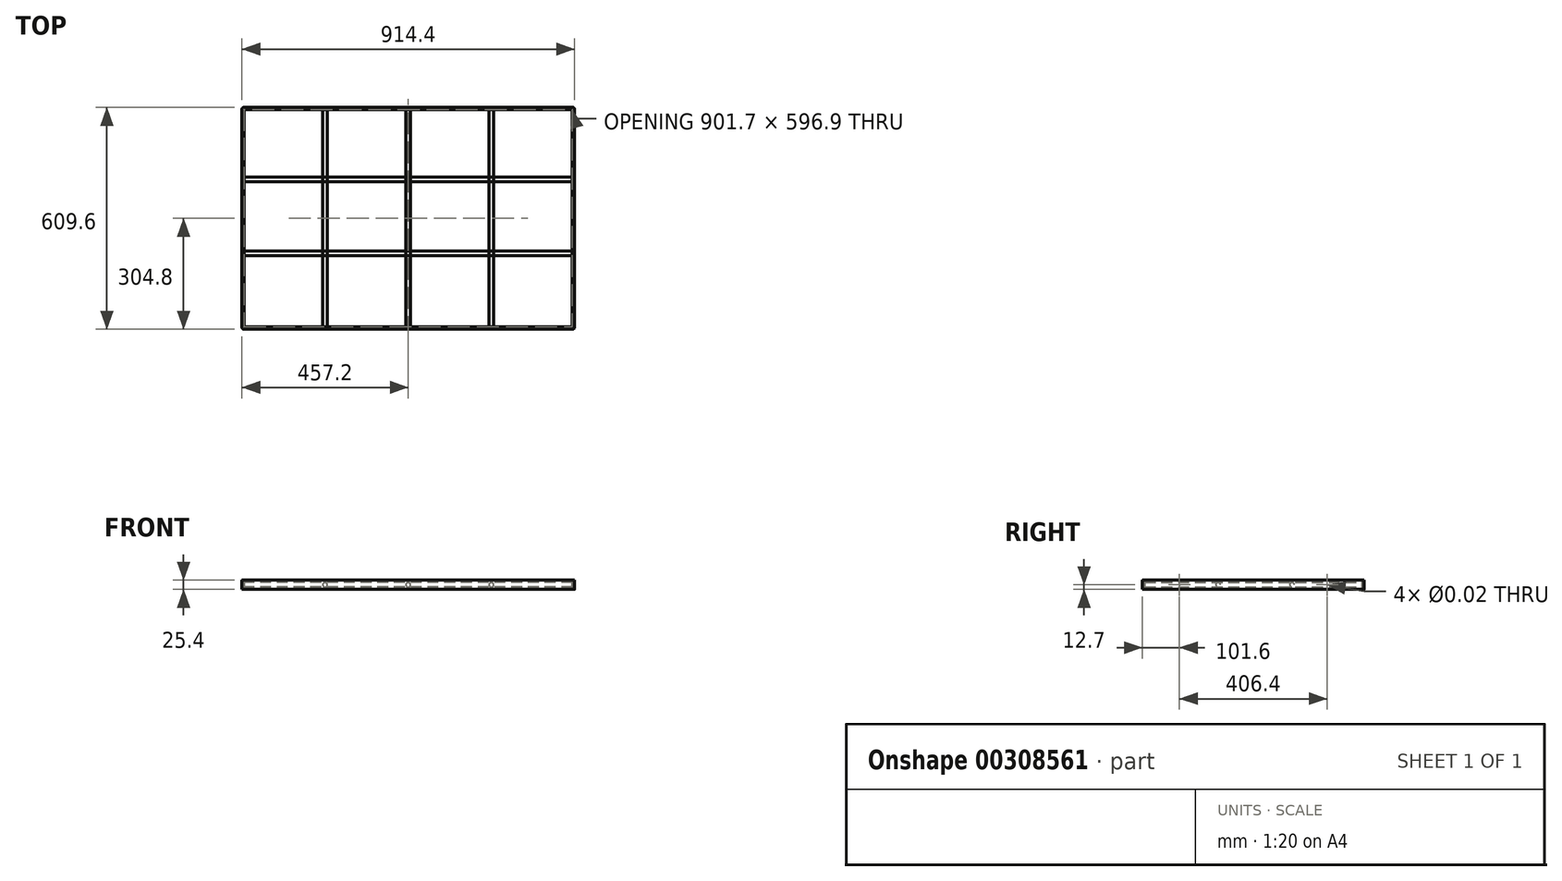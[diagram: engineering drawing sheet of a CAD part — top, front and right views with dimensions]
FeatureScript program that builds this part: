
annotation { "Feature Type Name" : "Feature", "Feature Type Description" : "" }
export const myFeature = defineFeature(function(context is Context, id is Id, definition is map)
    precondition{}
    {
        {
            var Q0;
            Q0=qCreatedBy(makeId("Top.planeOp"),FACE);
            var sketch = newSketch(context, id + "F0", { "sketchPlane" : qUnion([Q0])});
            skLineSegment(sketch, "E0.bottom", {"start": v(0, 0) * mm, "end": v(914.4, 0) * mm});
            skLineSegment(sketch, "E0.top", {"start": v(0, -609.6) * mm, "end": v(914.4, -609.6) * mm});
            skLineSegment(sketch, "E0.left", {"start": v(0, 0) * mm, "end": v(0, -609.6) * mm});
            skLineSegment(sketch, "E0.right", {"start": v(914.4, 0) * mm, "end": v(914.4, -609.6) * mm});
            skLineSegment(sketch, "E1.0", {"start": v(6.35, -6.35) * mm, "end": v(908.05, -6.35) * mm});
            skLineSegment(sketch, "E1.1", {"start": v(6.35, -6.35) * mm, "end": v(6.35, -603.25) * mm});
            skLineSegment(sketch, "E1.2", {"start": v(6.35, -603.25) * mm, "end": v(908.05, -603.25) * mm});
            skLineSegment(sketch, "E1.3", {"start": v(908.05, -6.35) * mm, "end": v(908.05, -603.25) * mm});
            skSolve(sketch);
        }
        {
            var Q0;
            Q0=makeQuery(id+"F0.imprint","IMPRINT",FACE,{"disambiguationData":[TD([[makeQuery(id+"F0.imprint","IMPRINT",EDGE,{"derivedFrom":sQuery(id+"F0.wireOp",EDGE,"E0.bottom")}),-1.0]])]});
            extrude(context, id + "F1", {"entities" : qUnion([Q0]), "depth" : 25.4 * mm});
        }
        {
            var Q0;
            Q0=makeQuery(id+"F1.opExtrude","SWEPT_EDGE",EDGE,{"disambiguationData":[OSD([sQuery(id+"F0.wireOp",EDGE,"E0.bottom"),sQuery(id+"F0.wireOp",EDGE,"E0.right")])]});
            var Q1;
            Q1=makeQuery(id+"F1.opExtrude","SWEPT_EDGE",EDGE,{"disambiguationData":[OSD([sQuery(id+"F0.wireOp",EDGE,"E1.2"),sQuery(id+"F0.wireOp",EDGE,"E1.3")])]});
            var Q2;
            Q2=makeQuery(id+"F1.opExtrude","SWEPT_EDGE",EDGE,{"disambiguationData":[OSD([sQuery(id+"F0.wireOp",EDGE,"E0.bottom"),sQuery(id+"F0.wireOp",EDGE,"E0.left")])]});
            var Q3;
            Q3=makeQuery(id+"F1.opExtrude","SWEPT_EDGE",EDGE,{"disambiguationData":[OSD([sQuery(id+"F0.wireOp",EDGE,"E1.1"),sQuery(id+"F0.wireOp",EDGE,"E1.2")])]});
            var Q4;
            Q4=makeQuery(id+"F1.opExtrude","SWEPT_EDGE",EDGE,{"disambiguationData":[OSD([sQuery(id+"F0.wireOp",EDGE,"E0.top"),sQuery(id+"F0.wireOp",EDGE,"E0.right")])]});
            var Q5;
            Q5=makeQuery(id+"F1.opExtrude","SWEPT_EDGE",EDGE,{"disambiguationData":[OSD([sQuery(id+"F0.wireOp",EDGE,"E0.top"),sQuery(id+"F0.wireOp",EDGE,"E0.left")])]});
            var Q6;
            Q6=makeQuery(id+"F1.opExtrude","SWEPT_EDGE",EDGE,{"disambiguationData":[OSD([sQuery(id+"F0.wireOp",EDGE,"E1.0"),sQuery(id+"F0.wireOp",EDGE,"E1.3")])]});
            var Q7;
            Q7=makeQuery(id+"F1.opExtrude","SWEPT_EDGE",EDGE,{"disambiguationData":[OSD([sQuery(id+"F0.wireOp",EDGE,"E1.0"),sQuery(id+"F0.wireOp",EDGE,"E1.1")])]});
            fillet(context, id + "F2", {"entities" : qUnion([Q0, Q1, Q2, Q3, Q4, Q5, Q6, Q7]), "radius" : 5.08 * mm, "tangentPropagation" : true, "allowEdgeOverflow" : false});
        }
        {
            var Q0;
            Q0=makeQuery(id+"F1.opExtrude","SWEPT_FACE",FACE,{"disambiguationData":[OSD([sQuery(id+"F0.wireOp",EDGE,"E1.1")])]});
            var sketch = newSketch(context, id + "F3", { "sketchPlane" : qUnion([Q0])});
            skCircle(sketch, "E2", {"center": v(-401.32, 12.7) * mm, "radius": 6.35 * mm});
            skCircle(sketch, "E3", {"center": v(-198.12, 12.7) * mm, "radius": 6.35 * mm});
            skSolve(sketch);
        }
        {
            var Q0;
            Q0 = qSketchRegion(id + "F3", true);
            var Q1;
            Q1=sQuery(id+"F3.wireOp",EDGE,"E3");
            var Q2;
            Q2=sQuery(id+"F3.wireOp",EDGE,"E2");
            extrude(context, id + "F4", {"entities" : qUnion([Q0]), "surfaceEntities" : qUnion([Q1, Q2]), "endBound" : BoundingType.UP_TO_NEXT, "depth" : 25.4 * mm});
        }
        {
            var Q0;
            Q0=makeQuery(id+"F1.opExtrude","SWEPT_FACE",FACE,{"disambiguationData":[OSD([sQuery(id+"F0.wireOp",EDGE,"E1.0")])]});
            var sketch = newSketch(context, id + "F5", { "sketchPlane" : qUnion([Q0])});
            skCircle(sketch, "E4", {"center": v(228.6, 12.7) * mm, "radius": 6.35 * mm});
            skCircle(sketch, "E5", {"center": v(457.2, 12.7) * mm, "radius": 6.35 * mm});
            skCircle(sketch, "E6", {"center": v(685.8, 12.7) * mm, "radius": 6.35 * mm});
            skSolve(sketch);
        }
        {
            var Q0;
            Q0 = qSketchRegion(id + "F5", true);
            var Q1;
            Q1=sQuery(id+"F5.wireOp",EDGE,"E4");
            var Q2;
            Q2=sQuery(id+"F5.wireOp",EDGE,"E5");
            var Q3;
            Q3=sQuery(id+"F5.wireOp",EDGE,"E6");
            var Q4;
            Q4=makeQuery(id+"F1.opExtrude","SWEPT_FACE",FACE,{"disambiguationData":[OSD([sQuery(id+"F0.wireOp",EDGE,"E1.2")])]});
            extrude(context, id + "F6", {"entities" : qUnion([Q0]), "surfaceEntities" : qUnion([Q1, Q2, Q3]), "endBound" : BoundingType.UP_TO_SURFACE, "endBoundEntityFace" : qUnion([Q4]), "depth" : 25.4 * mm});
        }
        {
            var Q0;
            Q0=makeQuery(id+"F1.opExtrude","SWEPT_FACE",FACE,{"disambiguationData":[OSD([sQuery(id+"F0.wireOp",EDGE,"E0.left")])]});
            var sketch = newSketch(context, id + "F7", { "sketchPlane" : qUnion([Q0])});
            skPoint(sketch, "E7", {"position": v(101.6, 12.7) * mm});
            skPoint(sketch, "E8", {"position": v(783.57, 10.27) * mm});
            skPoint(sketch, "E9", {"position": v(508, 12.7) * mm});
            skSolve(sketch);
        }
        {
            var Q0;
            Q0=sQuery(id+"F7.wireOp",VERTEX,"E7");
            var Q1;
            Q1=sQuery(id+"F7.wireOp",VERTEX,"E9");
            var Q2;
            Q2=makeQuery(id+"F1.opExtrude","SWEPT_BODY",BODY,{"disambiguationData":[OSD([sQuery(id+"F0.wireOp",EDGE,"E0.bottom"),sQuery(id+"F0.wireOp",EDGE,"E0.top"),sQuery(id+"F0.wireOp",EDGE,"E0.left"),sQuery(id+"F0.wireOp",EDGE,"E0.right"),sQuery(id+"F0.wireOp",EDGE,"E1.0"),sQuery(id+"F0.wireOp",EDGE,"E1.1"),sQuery(id+"F0.wireOp",EDGE,"E1.2"),sQuery(id+"F0.wireOp",EDGE,"E1.3")])]});
            hole(context, id + "F8", {"style" : HoleStyle.SIMPLE, "endStyle" : HoleEndStyle.BLIND, "standardTappedOrClearance" : lookupTablePath({ "standard" : "ANSI", "size" : "1/2 (0.5)", "type" : "Drilled" }), "standardBlindInLast" : lookupTablePath({ "standard" : "ANSI", "size" : "1/2", "type" : "Drilled" }), "holeDiameter" : 1 / 50.8 * mm, "holeDepth" : 6.35 * mm, "tappedDepth" : 12.7 * mm, "tapClearance" : 3, "locations" : qUnion([Q0, Q1]), "scope" : qUnion([Q2])});
        }
        {
            var Q0;
            Q0=makeQuery(id+"F1.opExtrude","SWEPT_FACE",FACE,{"disambiguationData":[OSD([sQuery(id+"F0.wireOp",EDGE,"E0.right")])]});
            var sketch = newSketch(context, id + "F9", { "sketchPlane" : qUnion([Q0])});
            skPoint(sketch, "E10", {"position": v(-508, 12.7) * mm});
            skPoint(sketch, "E11", {"position": v(-101.6, 12.7) * mm});
            skSolve(sketch);
        }
        {
            var Q0;
            Q0=sQuery(id+"F9.wireOp",VERTEX,"E10");
            var Q1;
            Q1=sQuery(id+"F9.wireOp",VERTEX,"E11");
            var Q2;
            Q2=makeQuery(id+"F1.opExtrude","SWEPT_BODY",BODY,{"disambiguationData":[OSD([sQuery(id+"F0.wireOp",EDGE,"E0.bottom"),sQuery(id+"F0.wireOp",EDGE,"E0.top"),sQuery(id+"F0.wireOp",EDGE,"E0.left"),sQuery(id+"F0.wireOp",EDGE,"E0.right"),sQuery(id+"F0.wireOp",EDGE,"E1.0"),sQuery(id+"F0.wireOp",EDGE,"E1.1"),sQuery(id+"F0.wireOp",EDGE,"E1.2"),sQuery(id+"F0.wireOp",EDGE,"E1.3")])]});
            hole(context, id + "F10", {"style" : HoleStyle.SIMPLE, "endStyle" : HoleEndStyle.BLIND, "standardTappedOrClearance" : lookupTablePath({ "standard" : "ANSI", "size" : "1/2 (0.5)", "type" : "Drilled" }), "standardBlindInLast" : lookupTablePath({ "standard" : "ANSI", "size" : "1/2", "type" : "Drilled" }), "holeDiameter" : 1 / 50.8 * mm, "holeDepth" : 6.35 * mm, "tappedDepth" : 12.7 * mm, "tapClearance" : 3, "locations" : qUnion([Q0, Q1]), "scope" : qUnion([Q2])});
        }
    });
